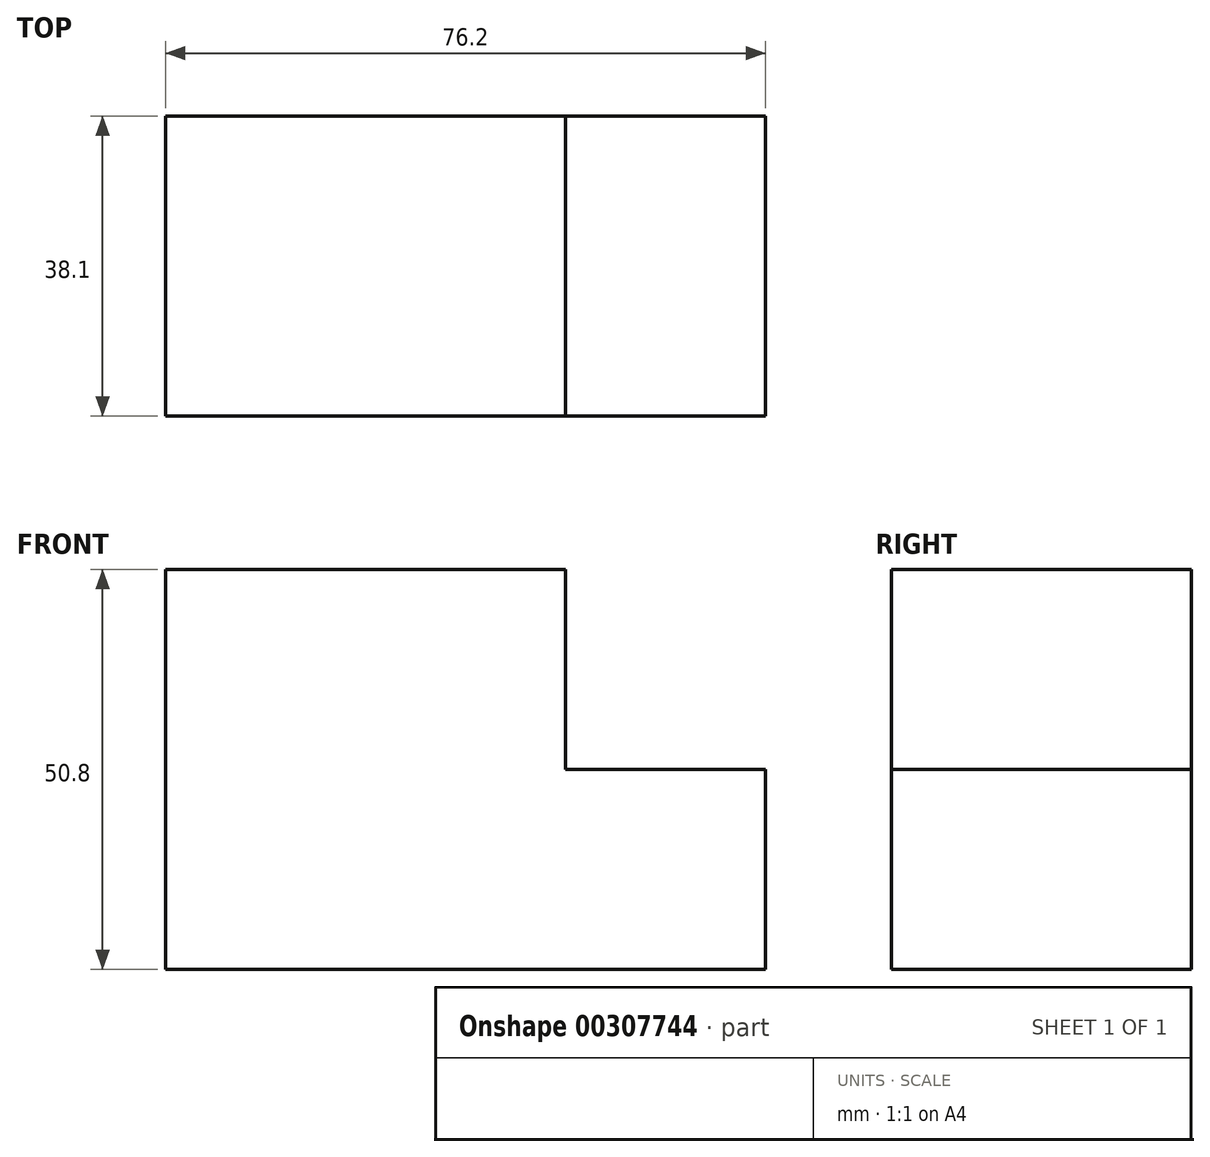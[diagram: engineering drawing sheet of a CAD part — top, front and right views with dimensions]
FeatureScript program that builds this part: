
annotation { "Feature Type Name" : "Feature", "Feature Type Description" : "" }
export const myFeature = defineFeature(function(context is Context, id is Id, definition is map)
    precondition{}
    {
        {
            var Q0;
            Q0=qCreatedBy(makeId("Front.planeOp"),FACE);
            var sketch = newSketch(context, id + "F0", { "sketchPlane" : qUnion([Q0])});
            skLineSegment(sketch, "E0", {"start": v(-47.23, -49.16) * mm, "end": v(28.97, -49.16) * mm});
            skLineSegment(sketch, "E1", {"start": v(28.97, -49.16) * mm, "end": v(28.97, -23.76) * mm});
            skLineSegment(sketch, "E2", {"start": v(28.97, -23.76) * mm, "end": v(3.57, -23.76) * mm});
            skLineSegment(sketch, "E3", {"start": v(3.57, -23.76) * mm, "end": v(3.57, 1.64) * mm});
            skLineSegment(sketch, "E4", {"start": v(3.57, 1.64) * mm, "end": v(-47.23, 1.64) * mm});
            skLineSegment(sketch, "E5", {"start": v(-47.23, 1.64) * mm, "end": v(-47.23, -49.16) * mm});
            skSolve(sketch);
        }
        {
            var Q0;
            Q0=makeQuery(id+"F0.imprint","IMPRINT",FACE,{"disambiguationData":[TD([[makeQuery(id+"F0.imprint","IMPRINT",EDGE,{"derivedFrom":sQuery(id+"F0.wireOp",EDGE,"E0")}),1.0]])]});
            extrude(context, id + "F1", {"entities" : qUnion([Q0]), "depth" : 38.1 * mm});
        }
    });
